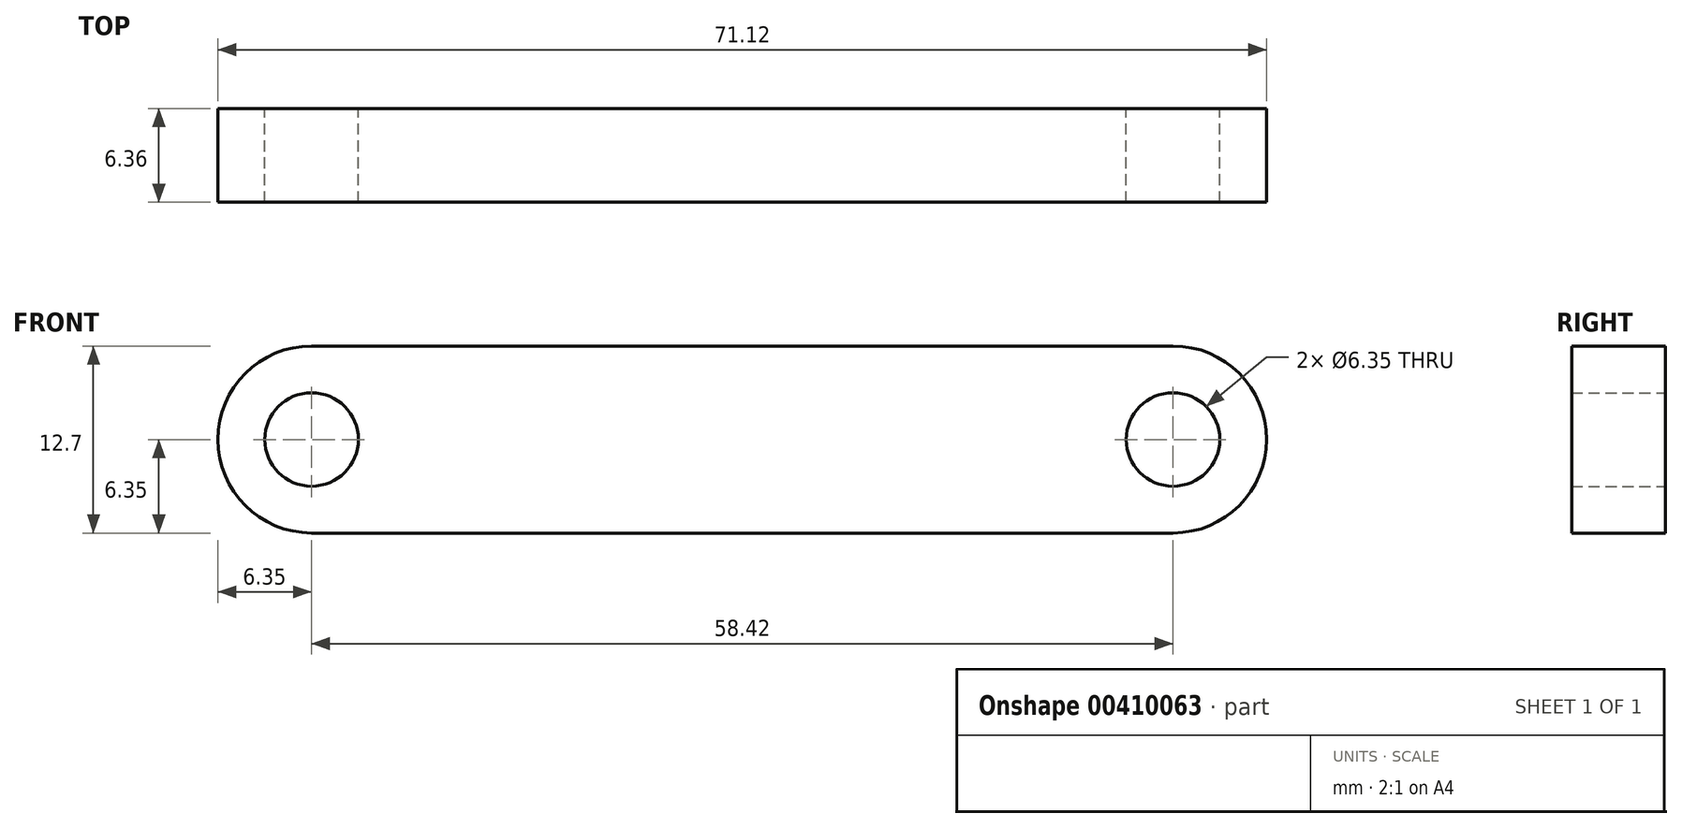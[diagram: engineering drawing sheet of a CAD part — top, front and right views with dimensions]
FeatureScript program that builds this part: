
annotation { "Feature Type Name" : "Feature", "Feature Type Description" : "" }
export const myFeature = defineFeature(function(context is Context, id is Id, definition is map)
    precondition{}
    {
        {
            var Q0;
            Q0=qCreatedBy(makeId("Front.planeOp"),FACE);
            var sketch = newSketch(context, id + "F0", { "sketchPlane" : qUnion([Q0])});
            skLineSegment(sketch, "E0", {"start": v(-29.08, 0) * mm, "end": v(32.08, 0) * mm, "construction": true});
            skLineSegment(sketch, "E1", {"start": v(0, 29) * mm, "end": v(0, -26.08) * mm, "construction": true});
            skLineSegment(sketch, "E2", {"start": v(-29.2, 8.23) * mm, "end": v(-29.2, -7.3) * mm, "construction": true});
            skCircle(sketch, "E3", {"center": v(-29.2, 0) * mm, "radius": 3.18 * mm});
            skArc(sketch, "E4", {"start": v(-29.2, 6.35) * mm, "mid": v(-35.56, 0) * mm, "end": v(-29.2, -6.35) * mm});
            skLineSegment(sketch, "E5", {"start": v(-29.2, 6.35) * mm, "end": v(0, 6.35) * mm});
            skLineSegment(sketch, "E6", {"start": v(-29.2, -6.35) * mm, "end": v(0, -6.35) * mm});
            skLineSegment(sketch, "E7.MirrorCS", {"start": v(29.2, 6.35) * mm, "end": v(0, 6.35) * mm});
            skArc(sketch, "E8.MirrorCS", {"start": v(29.2, 6.35) * mm, "mid": v(35.56, 0) * mm, "end": v(29.2, -6.35) * mm});
            skCircle(sketch, "E9.MirrorC", {"center": v(29.2, 0) * mm, "radius": 3.18 * mm});
            skLineSegment(sketch, "E10.MirrorCS", {"start": v(29.2, -6.35) * mm, "end": v(0, -6.35) * mm});
            skSolve(sketch);
        }
        {
            var Q0;
            Q0 = qSketchRegion(id + "F0", true);
            extrude(context, id + "F1", {"entities" : qUnion([Q0]), "endBound" : BoundingType.SYMMETRIC, "depth" : 6.35 * mm});
        }
    });
